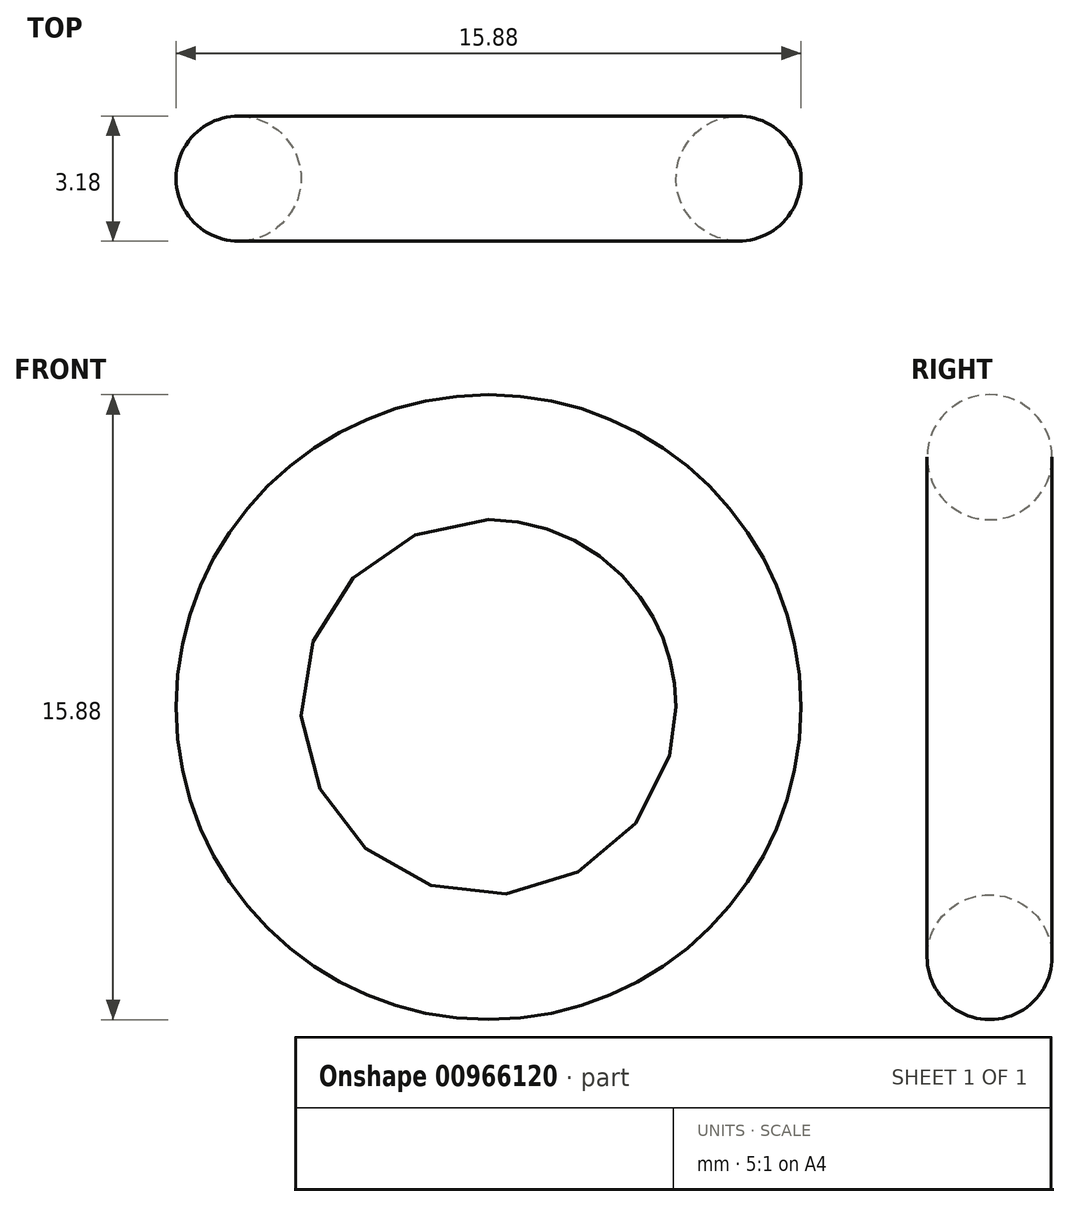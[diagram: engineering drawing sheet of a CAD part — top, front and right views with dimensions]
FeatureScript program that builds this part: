
annotation { "Feature Type Name" : "Feature", "Feature Type Description" : "" }
export const myFeature = defineFeature(function(context is Context, id is Id, definition is map)
    precondition{}
    {
        {
            var Q0;
            Q0=qCreatedBy(makeId("Top.planeOp"),FACE);
            var sketch = newSketch(context, id + "F0", { "sketchPlane" : qUnion([Q0])});
            skLineSegment(sketch, "E0", {"start": v(0, 6.5) * mm, "end": v(0, -8.4) * mm});
            skCircle(sketch, "E1", {"center": v(-6.35, 0) * mm, "radius": 1.59 * mm});
            skSolve(sketch);
        }
        {
            var Q0;
            Q0=makeQuery(id+"F0.imprint","IMPRINT",FACE,{"disambiguationData":[TD([[makeQuery(id+"F0.imprint","IMPRINT",EDGE,{"derivedFrom":sQuery(id+"F0.wireOp",EDGE,"E1")}),1.0]])]});
            var Q1;
            Q1=sQuery(id+"F0.wireOp",EDGE,"E0");
            revolve(context, id + "F1", {"surfaceOperationType" : NewSurfaceOperationType.NEW, "entities" : qUnion([Q0]), "axis" : qUnion([Q1]), "revolveType" : RevolveType.FULL});
        }
    });
